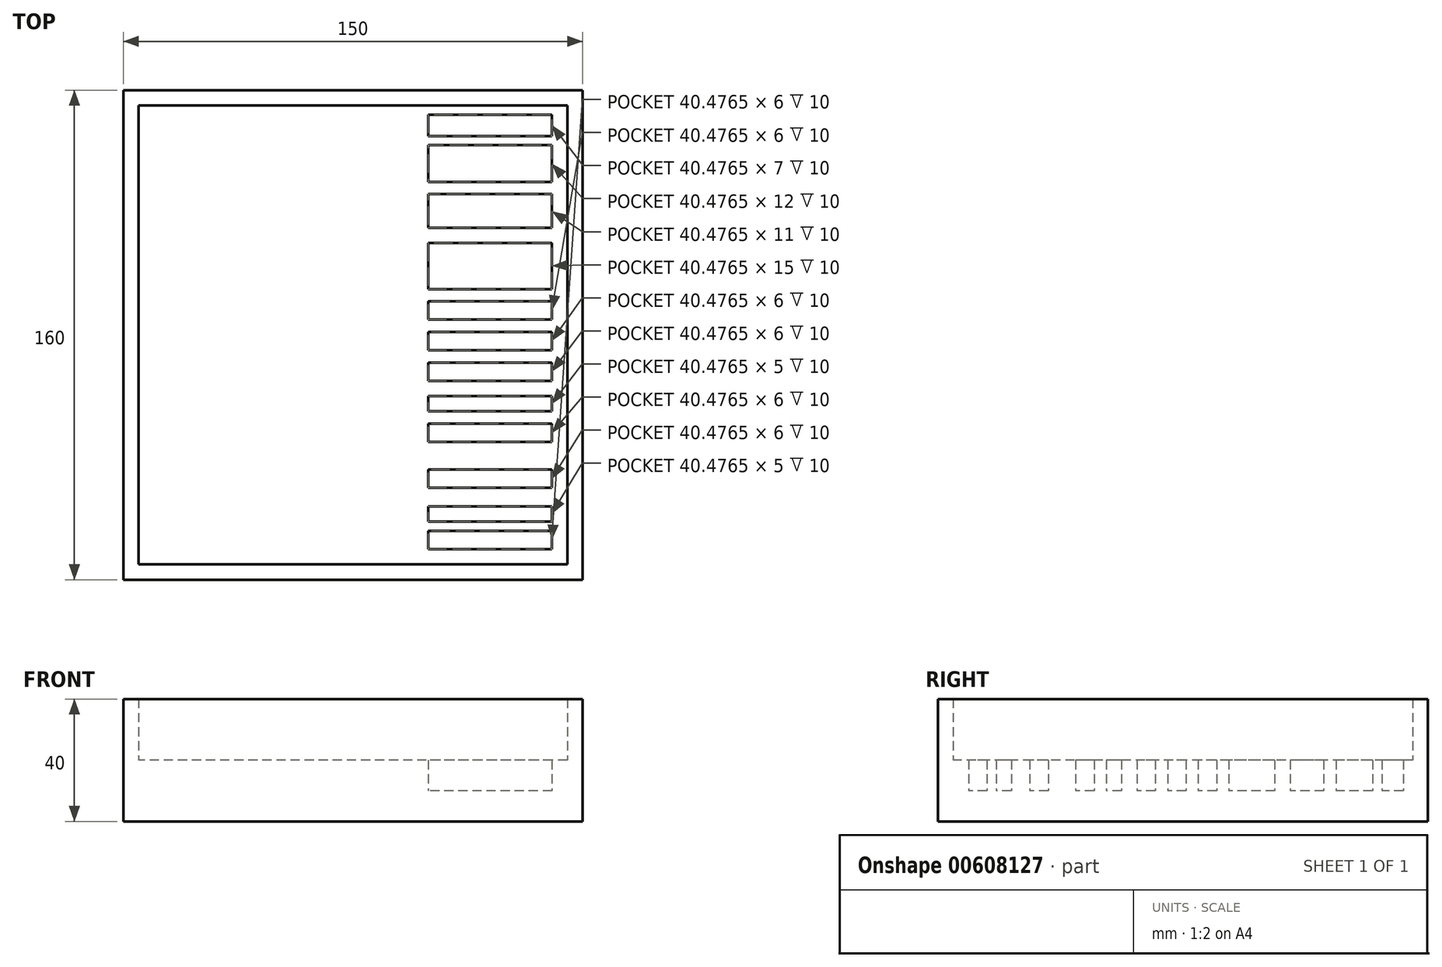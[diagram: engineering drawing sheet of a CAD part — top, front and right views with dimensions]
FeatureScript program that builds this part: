
annotation { "Feature Type Name" : "Feature", "Feature Type Description" : "" }
export const myFeature = defineFeature(function(context is Context, id is Id, definition is map)
    precondition{}
    {
        {
            var Q0;
            Q0=qCreatedBy(makeId("Top.planeOp"),FACE);
            var sketch = newSketch(context, id + "F0", { "sketchPlane" : qUnion([Q0])});
            skLineSegment(sketch, "E0.bottom", {"start": v(75, 80) * mm, "end": v(-75, 80) * mm});
            skLineSegment(sketch, "E0.top", {"start": v(75, -80) * mm, "end": v(-75, -80) * mm});
            skLineSegment(sketch, "E0.left", {"start": v(75, 80) * mm, "end": v(75, -80) * mm});
            skLineSegment(sketch, "E0.right", {"start": v(-75, 80) * mm, "end": v(-75, -80) * mm});
            skPoint(sketch, "E0.middle", {"position": v(0, 0) * mm});
            skSolve(sketch);
        }
        {
            var Q0;
            Q0 = qSketchRegion(id + "F0", true);
            extrude(context, id + "F1", {"entities" : qUnion([Q0]), "depth" : 10 * mm, "offsetDistance" : 25 * mm});
        }
        {
            var Q0;
            Q0=makeQuery(id+"F1.opExtrude","CAP_FACE",FACE,{"disambiguationData":[OSD([sQuery(id+"F0.wireOp",EDGE,"E0.bottom"),sQuery(id+"F0.wireOp",EDGE,"E0.top"),sQuery(id+"F0.wireOp",EDGE,"E0.left"),sQuery(id+"F0.wireOp",EDGE,"E0.right")])],"isStart":false});
            var sketch = newSketch(context, id + "F2", { "sketchPlane" : qUnion([Q0])});
            skLineSegment(sketch, "E1.0", {"start": v(-75, 80) * mm, "end": v(-75, -80) * mm});
            skLineSegment(sketch, "E2.0", {"start": v(75, -80) * mm, "end": v(-75, -80) * mm});
            skLineSegment(sketch, "E3.0.0", {"start": v(75, -80) * mm, "end": v(75, 80) * mm});
            skLineSegment(sketch, "E3.0.2", {"start": v(75, 80) * mm, "end": v(75, -80) * mm});
            skLineSegment(sketch, "E4.0", {"start": v(75, 80) * mm, "end": v(-75, 80) * mm});
            skLineSegment(sketch, "E5.bottom", {"start": v(70, 75) * mm, "end": v(-70, 75) * mm});
            skLineSegment(sketch, "E5.top", {"start": v(70, -75) * mm, "end": v(-70, -75) * mm});
            skLineSegment(sketch, "E5.left", {"start": v(70, 75) * mm, "end": v(70, -75) * mm});
            skLineSegment(sketch, "E5.right", {"start": v(-70, 75) * mm, "end": v(-70, -75) * mm});
            skPoint(sketch, "E5.middle", {"position": v(0, 0) * mm});
            skSolve(sketch);
        }
        {
            var Q0;
            Q0 = qSketchRegion(id + "F2", true);
            extrude(context, id + "F3", {"entities" : qUnion([Q0]), "operationType" : NewBodyOperationType.ADD, "depth" : 30 * mm, "offsetDistance" : 25 * mm});
        }
        {
            var Q0;
            Q0=makeQuery(id+"F1.opExtrude","CAP_FACE",FACE,{"disambiguationData":[OSD([sQuery(id+"F0.wireOp",EDGE,"E0.bottom"),sQuery(id+"F0.wireOp",EDGE,"E0.top"),sQuery(id+"F0.wireOp",EDGE,"E0.left"),sQuery(id+"F0.wireOp",EDGE,"E0.right")])],"isStart":false});
            var sketch = newSketch(context, id + "F4", { "sketchPlane" : qUnion([Q0])});
            skLineSegment(sketch, "E6.bottom", {"start": v(65, -64) * mm, "end": v(24.52, -64) * mm});
            skLineSegment(sketch, "E6.top", {"start": v(65, -70) * mm, "end": v(24.52, -70) * mm});
            skLineSegment(sketch, "E6.left", {"start": v(65, -64) * mm, "end": v(65, -70) * mm});
            skLineSegment(sketch, "E6.right", {"start": v(24.52, -64) * mm, "end": v(24.52, -70) * mm});
            skPoint(sketch, "E6.middle", {"position": v(44.76, -67) * mm});
            skLineSegment(sketch, "E7.bottom", {"start": v(65, -56) * mm, "end": v(24.52, -56) * mm});
            skLineSegment(sketch, "E7.top", {"start": v(65, -61) * mm, "end": v(24.52, -61) * mm});
            skLineSegment(sketch, "E7.left", {"start": v(65, -56) * mm, "end": v(65, -61) * mm});
            skLineSegment(sketch, "E7.right", {"start": v(24.52, -56) * mm, "end": v(24.52, -61) * mm});
            skPoint(sketch, "E7.middle", {"position": v(44.76, -58.5) * mm});
            skLineSegment(sketch, "E8.bottom", {"start": v(65, -44) * mm, "end": v(24.52, -44) * mm});
            skLineSegment(sketch, "E8.top", {"start": v(65, -50) * mm, "end": v(24.52, -50) * mm});
            skLineSegment(sketch, "E8.left", {"start": v(65, -44) * mm, "end": v(65, -50) * mm});
            skLineSegment(sketch, "E8.right", {"start": v(24.52, -44) * mm, "end": v(24.52, -50) * mm});
            skPoint(sketch, "E8.middle", {"position": v(44.76, -47) * mm});
            skLineSegment(sketch, "E9.bottom", {"start": v(65, -29) * mm, "end": v(24.52, -29) * mm});
            skLineSegment(sketch, "E9.top", {"start": v(65, -35) * mm, "end": v(24.52, -35) * mm});
            skLineSegment(sketch, "E9.left", {"start": v(65, -29) * mm, "end": v(65, -35) * mm});
            skLineSegment(sketch, "E9.right", {"start": v(24.52, -29) * mm, "end": v(24.52, -35) * mm});
            skPoint(sketch, "E9.middle", {"position": v(44.76, -32) * mm});
            skLineSegment(sketch, "E10.bottom", {"start": v(65, -20) * mm, "end": v(24.52, -20) * mm});
            skLineSegment(sketch, "E10.top", {"start": v(65, -25) * mm, "end": v(24.52, -25) * mm});
            skLineSegment(sketch, "E10.left", {"start": v(65, -20) * mm, "end": v(65, -25) * mm});
            skLineSegment(sketch, "E10.right", {"start": v(24.52, -20) * mm, "end": v(24.52, -25) * mm});
            skPoint(sketch, "E10.middle", {"position": v(44.76, -22.5) * mm});
            skLineSegment(sketch, "E11.bottom", {"start": v(65, -9) * mm, "end": v(24.52, -9) * mm});
            skLineSegment(sketch, "E11.top", {"start": v(65, -15) * mm, "end": v(24.52, -15) * mm});
            skLineSegment(sketch, "E11.left", {"start": v(65, -9) * mm, "end": v(65, -15) * mm});
            skLineSegment(sketch, "E11.right", {"start": v(24.52, -9) * mm, "end": v(24.52, -15) * mm});
            skPoint(sketch, "E11.middle", {"position": v(44.76, -12) * mm});
            skLineSegment(sketch, "E12.bottom", {"start": v(65, 1) * mm, "end": v(24.52, 1) * mm});
            skLineSegment(sketch, "E12.top", {"start": v(65, -5) * mm, "end": v(24.52, -5) * mm});
            skLineSegment(sketch, "E12.left", {"start": v(65, 1) * mm, "end": v(65, -5) * mm});
            skLineSegment(sketch, "E12.right", {"start": v(24.52, 1) * mm, "end": v(24.52, -5) * mm});
            skPoint(sketch, "E12.middle", {"position": v(44.76, -2) * mm});
            skLineSegment(sketch, "E13.top", {"start": v(65, 5) * mm, "end": v(24.52, 5) * mm});
            skPoint(sketch, "E13.middle", {"position": v(44.76, 8) * mm});
            skLineSegment(sketch, "E14.bottom", {"start": v(65, 30) * mm, "end": v(24.52, 30) * mm});
            skLineSegment(sketch, "E14.top", {"start": v(65, 15) * mm, "end": v(24.52, 15) * mm});
            skLineSegment(sketch, "E14.left", {"start": v(65, 30) * mm, "end": v(65, 15) * mm});
            skLineSegment(sketch, "E14.right", {"start": v(24.52, 30) * mm, "end": v(24.52, 15) * mm});
            skPoint(sketch, "E14.middle", {"position": v(44.76, 22.5) * mm});
            skLineSegment(sketch, "E15.bottom", {"start": v(65, 46) * mm, "end": v(24.52, 46) * mm});
            skLineSegment(sketch, "E15.top", {"start": v(65, 35) * mm, "end": v(24.52, 35) * mm});
            skLineSegment(sketch, "E15.left", {"start": v(65, 46) * mm, "end": v(65, 35) * mm});
            skLineSegment(sketch, "E15.right", {"start": v(24.52, 46) * mm, "end": v(24.52, 35) * mm});
            skPoint(sketch, "E15.middle", {"position": v(44.76, 40.5) * mm});
            skLineSegment(sketch, "E16.bottom", {"start": v(65, 62) * mm, "end": v(24.52, 62) * mm});
            skLineSegment(sketch, "E16.top", {"start": v(65, 50) * mm, "end": v(24.52, 50) * mm});
            skLineSegment(sketch, "E16.left", {"start": v(65, 62) * mm, "end": v(65, 50) * mm});
            skLineSegment(sketch, "E16.right", {"start": v(24.52, 62) * mm, "end": v(24.52, 50) * mm});
            skPoint(sketch, "E16.middle", {"position": v(44.76, 56) * mm});
            skLineSegment(sketch, "E17.bottom", {"start": v(65, 72) * mm, "end": v(24.52, 72) * mm});
            skLineSegment(sketch, "E17.top", {"start": v(65, 65) * mm, "end": v(24.52, 65) * mm});
            skLineSegment(sketch, "E17.left", {"start": v(65, 72) * mm, "end": v(65, 65) * mm});
            skLineSegment(sketch, "E17.right", {"start": v(24.52, 72) * mm, "end": v(24.52, 65) * mm});
            skPoint(sketch, "E17.middle", {"position": v(44.76, 68.5) * mm});
            skLineSegment(sketch, "E18", {"start": v(24.52, 5) * mm, "end": v(24.52, 11) * mm});
            skLineSegment(sketch, "E19", {"start": v(24.52, 11) * mm, "end": v(65, 11) * mm});
            skLineSegment(sketch, "E20", {"start": v(65, 11) * mm, "end": v(65, 5) * mm});
            skLineSegment(sketch, "E21.0", {"start": v(70, 75) * mm, "end": v(-70, 75) * mm});
            skLineSegment(sketch, "E22.0", {"start": v(70, 75) * mm, "end": v(70, -75) * mm});
            skLineSegment(sketch, "E23.0", {"start": v(70, -75) * mm, "end": v(-70, -75) * mm});
            skLineSegment(sketch, "E24.0", {"start": v(-70, 75) * mm, "end": v(-70, -75) * mm});
            skSolve(sketch);
        }
        {
            var Q0;
            Q0 = qSketchRegion(id + "F4", true);
            extrude(context, id + "F5", {"entities" : qUnion([Q0]), "operationType" : NewBodyOperationType.ADD, "depth" : 10 * mm, "offsetDistance" : 25 * mm});
        }
    });
